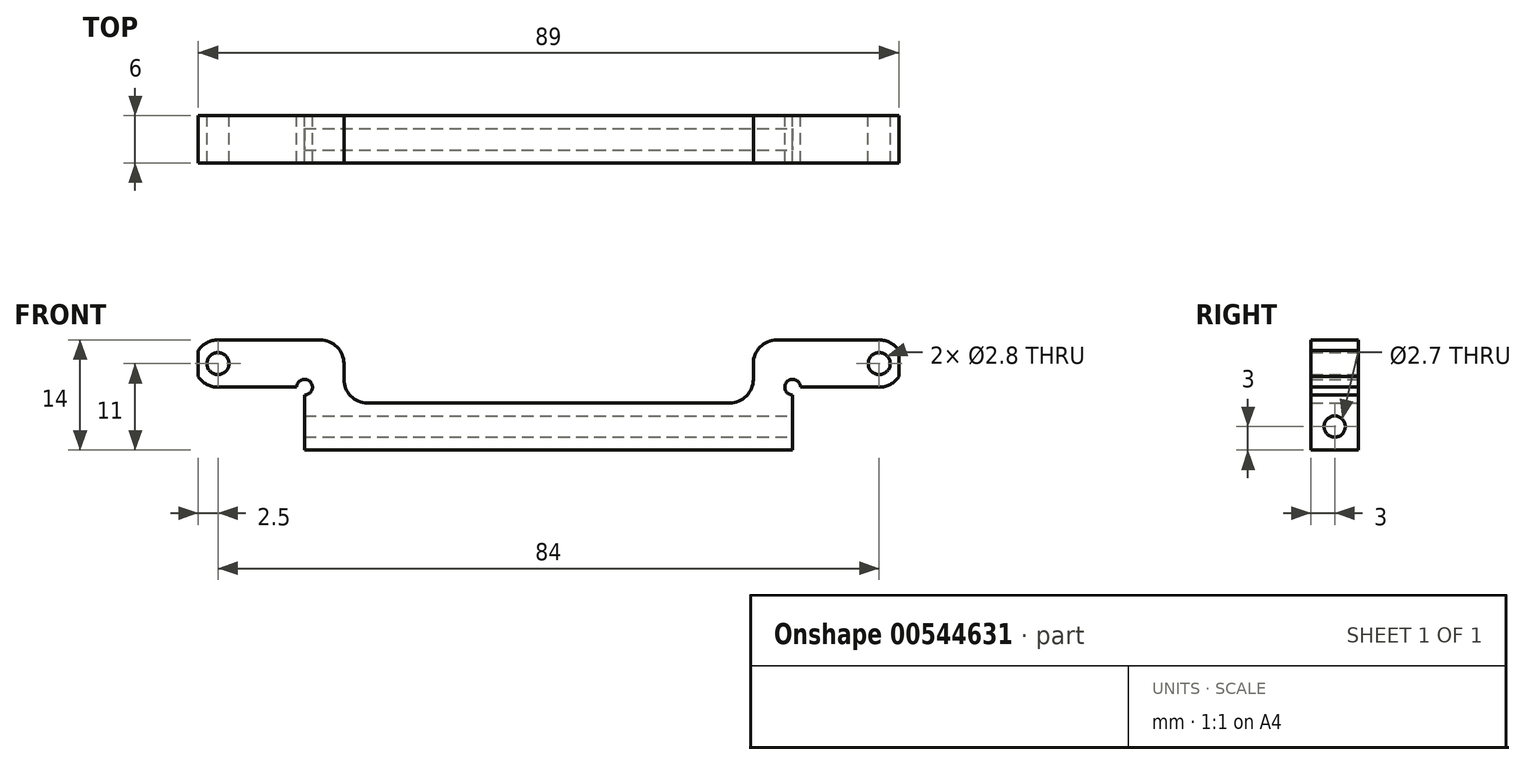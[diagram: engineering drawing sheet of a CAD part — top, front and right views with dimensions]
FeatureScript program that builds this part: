
annotation { "Feature Type Name" : "Feature", "Feature Type Description" : "" }
export const myFeature = defineFeature(function(context is Context, id is Id, definition is map)
    precondition{}
    {
        {
            var Q0;
            Q0=qCreatedBy(makeId("Front.planeOp"),FACE);
            var sketch = newSketch(context, id + "F0", { "sketchPlane" : qUnion([Q0])});
            skLineSegment(sketch, "E0.top", {"start": v(-31, -3) * mm, "end": v(31, -3) * mm});
            skLineSegment(sketch, "E0.left", {"start": v(-31, 4) * mm, "end": v(-31, -3) * mm});
            skLineSegment(sketch, "E0.right", {"start": v(31, 4) * mm, "end": v(31, -3) * mm});
            skLineSegment(sketch, "E1", {"start": v(32, 5) * mm, "end": v(42, 5) * mm});
            skLineSegment(sketch, "E2", {"start": v(44.5, 6.34) * mm, "end": v(44.5, 9.66) * mm});
            skLineSegment(sketch, "E3", {"start": v(42, 11) * mm, "end": v(26, 11) * mm});
            skLineSegment(sketch, "E4", {"start": v(26, 11) * mm, "end": v(26, 5) * mm});
            skCircle(sketch, "E5", {"center": v(42, 8) * mm, "radius": 1.4 * mm});
            skArc(sketch, "E6", {"start": v(44.5, 9.66) * mm, "mid": v(43.42, 10.64) * mm, "end": v(42, 11) * mm});
            skArc(sketch, "E7.trimOffspring", {"start": v(42, 5) * mm, "mid": v(43.42, 5.36) * mm, "end": v(44.5, 6.34) * mm});
            skLineSegment(sketch, "E8.MirrorCS", {"start": v(-26, 11) * mm, "end": v(-26, 5) * mm});
            skLineSegment(sketch, "E9.MirrorCS", {"start": v(-42, 11) * mm, "end": v(-26, 11) * mm});
            skLineSegment(sketch, "E10.MirrorCS", {"start": v(-32, 5) * mm, "end": v(-42, 5) * mm});
            skCircle(sketch, "E11.MirrorC", {"center": v(-42, 8) * mm, "radius": 1.4 * mm});
            skArc(sketch, "E12.MirrorCS", {"start": v(-44.5, 9.66) * mm, "mid": v(-43.42, 10.64) * mm, "end": v(-42, 11) * mm});
            skLineSegment(sketch, "E13.MirrorCS", {"start": v(-44.5, 6.34) * mm, "end": v(-44.5, 9.66) * mm});
            skArc(sketch, "E14.MirrorCS", {"start": v(-42, 5) * mm, "mid": v(-43.42, 5.36) * mm, "end": v(-44.5, 6.34) * mm});
            skArc(sketch, "E15", {"start": v(-31, 4) * mm, "mid": v(-30.3, 5.7) * mm, "end": v(-32, 5) * mm});
            skArc(sketch, "E16.MirrorCS", {"start": v(31, 4) * mm, "mid": v(30.3, 5.7) * mm, "end": v(32, 5) * mm});
            skLineSegment(sketch, "E17", {"start": v(-26, 5) * mm, "end": v(-26, 3) * mm});
            skLineSegment(sketch, "E18", {"start": v(-26, 3) * mm, "end": v(26, 3) * mm});
            skLineSegment(sketch, "E19", {"start": v(26, 3) * mm, "end": v(26, 5) * mm});
            skSolve(sketch);
        }
        {
            var Q0;
            Q0=makeQuery(id+"F0.imprint","IMPRINT",FACE,{"disambiguationData":[TD([[makeQuery(id+"F0.imprint","IMPRINT",EDGE,{"derivedFrom":sQuery(id+"F0.wireOp",EDGE,"E0.top")}),1.0]])]});
            extrude(context, id + "F1", {"entities" : qUnion([Q0]), "depth" : 6 * mm, "offsetDistance" : 25 * mm});
        }
        {
            var Q0;
            Q0=makeQuery(id+"F1.opExtrude","SWEPT_EDGE",EDGE,{"disambiguationData":[OSD([sQuery(id+"F0.wireOp",EDGE,"E8.MirrorCS"),sQuery(id+"F0.wireOp",EDGE,"E9.MirrorCS")])]});
            var Q1;
            Q1=makeQuery(id+"F1.opExtrude","SWEPT_EDGE",EDGE,{"disambiguationData":[OSD([sQuery(id+"F0.wireOp",EDGE,"E3"),sQuery(id+"F0.wireOp",EDGE,"E4")])]});
            var Q2;
            Q2=makeQuery(id+"F1.opExtrude","SWEPT_EDGE",EDGE,{"disambiguationData":[OSD([sQuery(id+"F0.wireOp",EDGE,"E17"),sQuery(id+"F0.wireOp",EDGE,"E18")])]});
            var Q3;
            Q3=makeQuery(id+"F1.opExtrude","SWEPT_EDGE",EDGE,{"disambiguationData":[OSD([sQuery(id+"F0.wireOp",EDGE,"E18"),sQuery(id+"F0.wireOp",EDGE,"E19")])]});
            fillet(context, id + "F2", {"entities" : qUnion([Q0, Q1, Q2, Q3]), "radius" : 3 * mm, "tangentPropagation" : true, "allowEdgeOverflow" : false});
        }
        {
            var Q0;
            Q0=makeQuery(id+"F1.opExtrude","SWEPT_FACE",FACE,{"disambiguationData":[OSD([sQuery(id+"F0.wireOp",EDGE,"E0.right")])]});
            var sketch = newSketch(context, id + "F3", { "sketchPlane" : qUnion([Q0])});
            skCircle(sketch, "E20", {"center": v(-3, 0) * mm, "radius": 1.35 * mm});
            skSolve(sketch);
        }
        {
            var Q0;
            Q0=makeQuery(id+"F3.imprint","IMPRINT",FACE,{"disambiguationData":[TD([[makeQuery(id+"F3.imprint","IMPRINT",EDGE,{"derivedFrom":sQuery(id+"F3.wireOp",EDGE,"E20")}),1.0]])]});
            extrude(context, id + "F4", {"entities" : qUnion([Q0]), "operationType" : NewBodyOperationType.REMOVE, "endBound" : BoundingType.THROUGH_ALL, "oppositeDirection" : true, "depth" : 25 * mm, "offsetDistance" : 25 * mm});
        }
    });
